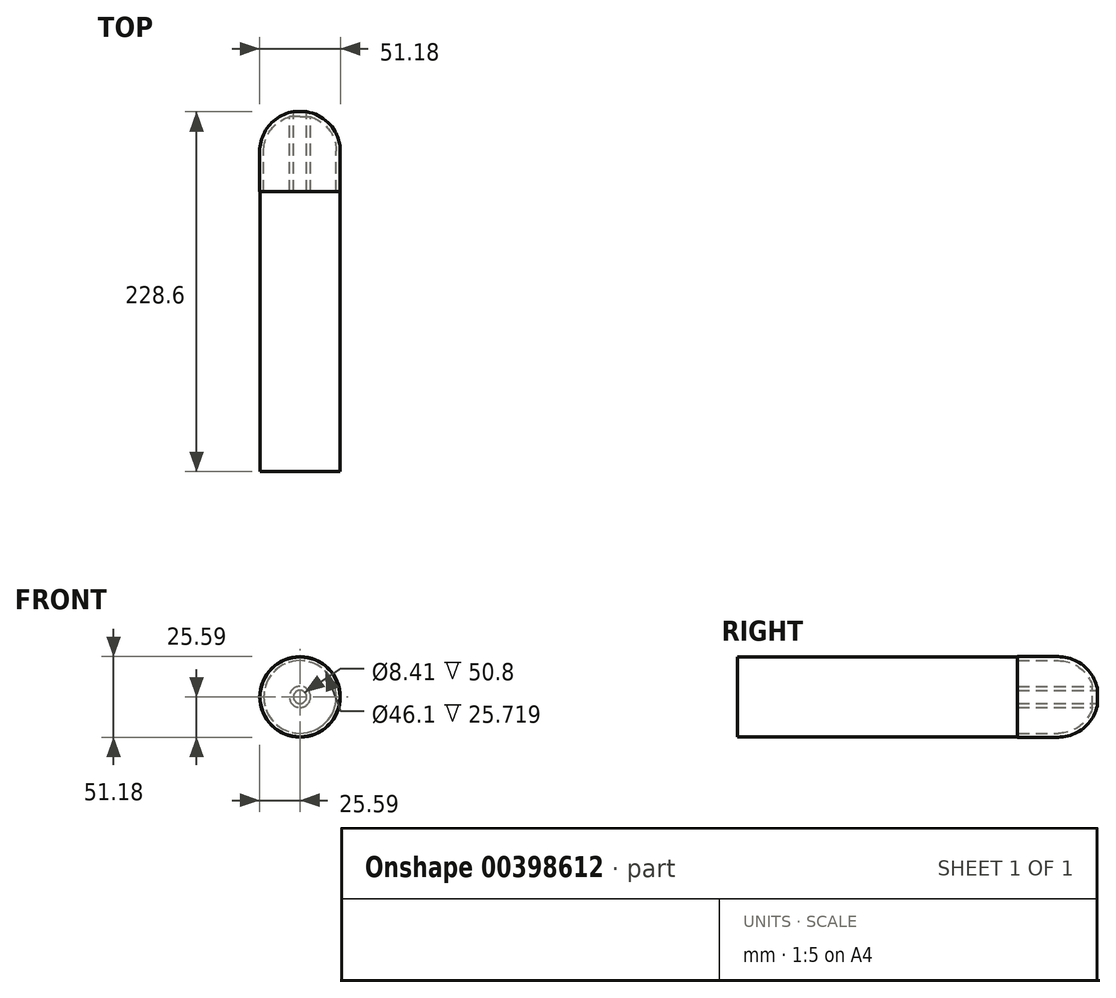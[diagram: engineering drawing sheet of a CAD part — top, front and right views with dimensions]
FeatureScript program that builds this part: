
annotation { "Feature Type Name" : "Feature", "Feature Type Description" : "" }
export const myFeature = defineFeature(function(context is Context, id is Id, definition is map)
    precondition{}
    {
        {
            var Q0;
            Q0=qCreatedBy(makeId("Front.planeOp"),FACE);
            var sketch = newSketch(context, id + "F0", { "sketchPlane" : qUnion([Q0])});
            skCircle(sketch, "E0", {"center": v(0, 0) * mm, "radius": 25.59 * mm});
            skCircle(sketch, "E1", {"center": v(0, 0) * mm, "radius": 4.2 * mm});
            skSolve(sketch);
        }
        {
            var Q0;
            Q0=makeQuery(id+"F0.imprint","IMPRINT",FACE,{"disambiguationData":[TD([[makeQuery(id+"F0.imprint","IMPRINT",EDGE,{"derivedFrom":sQuery(id+"F0.wireOp",EDGE,"E0")}),1.0]])]});
            extrude(context, id + "F1", {"entities" : qUnion([Q0]), "depth" : 50.8 * mm});
        }
        {
            var Q0;
            Q0=makeQuery(id+"F1.opExtrude","CAP_EDGE",EDGE,{"disambiguationData":[OSD([sQuery(id+"F0.wireOp",EDGE,"E0")])],"isStart":true});
            fillet(context, id + "F2", {"entities" : qUnion([Q0]), "radius" : 25.4 * mm, "tangentPropagation" : true, "allowEdgeOverflow" : false});
        }
        {
            var Q0;
            Q0=makeQuery(id+"F1.opExtrude","CAP_FACE",FACE,{"disambiguationData":[OSD([sQuery(id+"F0.wireOp",EDGE,"E0")])],"isStart":false});
            shell(context, id + "F3", {"entities" : qUnion([Q0]), "thickness" : 2.54 * mm});
        }
        {
            var Q0;
            Q0=makeQuery(id+"F1.opExtrude","CAP_FACE",FACE,{"disambiguationData":[OSD([sQuery(id+"F0.wireOp",EDGE,"E0"),sQuery(id+"F0.wireOp",EDGE,"E1")])],"isStart":false});
            var sketch = newSketch(context, id + "F4", { "sketchPlane" : qUnion([Q0])});
            skCircle(sketch, "E2", {"center": v(0, 0) * mm, "radius": 25.36 * mm});
            skSolve(sketch);
        }
        {
            var Q0;
            Q0 = qSketchRegion(id + "F4", true);
            extrude(context, id + "F5", {"entities" : qUnion([Q0]), "operationType" : NewBodyOperationType.ADD, "depth" : 177.8 * mm});
        }
    });
